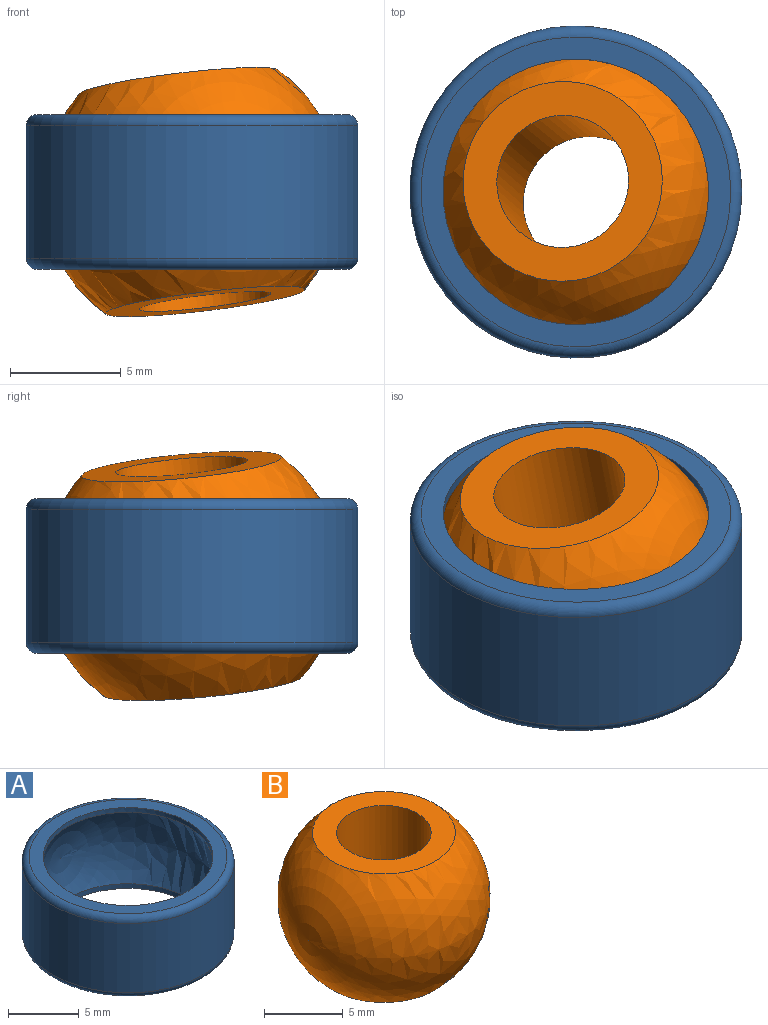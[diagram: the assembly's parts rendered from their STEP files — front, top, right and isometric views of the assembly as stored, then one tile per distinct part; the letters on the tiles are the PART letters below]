
ASSEMBLY  parts=2 mates=1
PART A: 8 faces, bbox 16.2x16.2x13.5 mm
  f0: cylinder r=6mm len=12mm, axis (0,0,-1), area 15.4mm2, adj f4,f5
  f1: cylinder r=6mm len=12mm, axis (0,0,-1), area 15.4mm2, adj f3,f5
  f2: cylinder r=7.5mm len=15mm, axis (0,0,-1), area 282.7mm2, adj f6,f7
  f3: plane 14x14mm, normal (0,0,1), area 40.8mm2, adj f1,f7
  f4: plane 14x14mm, normal (0,0,-1), area 40.8mm2, adj f0,f6
  f5: sphere r=6.75mm, area 262.4mm2, adj f0,f1
  f6: torus R=7mm, axis (0,0,1), area 36.1mm2, adj f2,f4
  f7: torus R=7mm, axis (0,0,1), area 36.1mm2, adj f2,f3
PART B: 4 faces, bbox 13.5x13.5x13.5 mm
  f0: cylinder r=3mm len=10mm, axis (0,0,1), area 188.5mm2, adj f1,f2
  f1: plane 9.07x9.07mm, normal (0,0,1), area 36.3mm2, adj f0,f3
  f2: plane 9.07x9.07mm, normal (0,0,-1), area 36.3mm2, adj f0,f3
  f3: sphere r=6.75mm, area 424.1mm2, adj f1,f2
PLACE A t=(1.49,-14.51,5)mm fixed
PLACE B rot(axis=(0.57,0.82,-0.01),171.3deg) t=(1.49,-14.51,5)mm
MATE ball A.f0 <-> B.f0  axis (0,0,1) through (1.49,-14.51,5)mm
